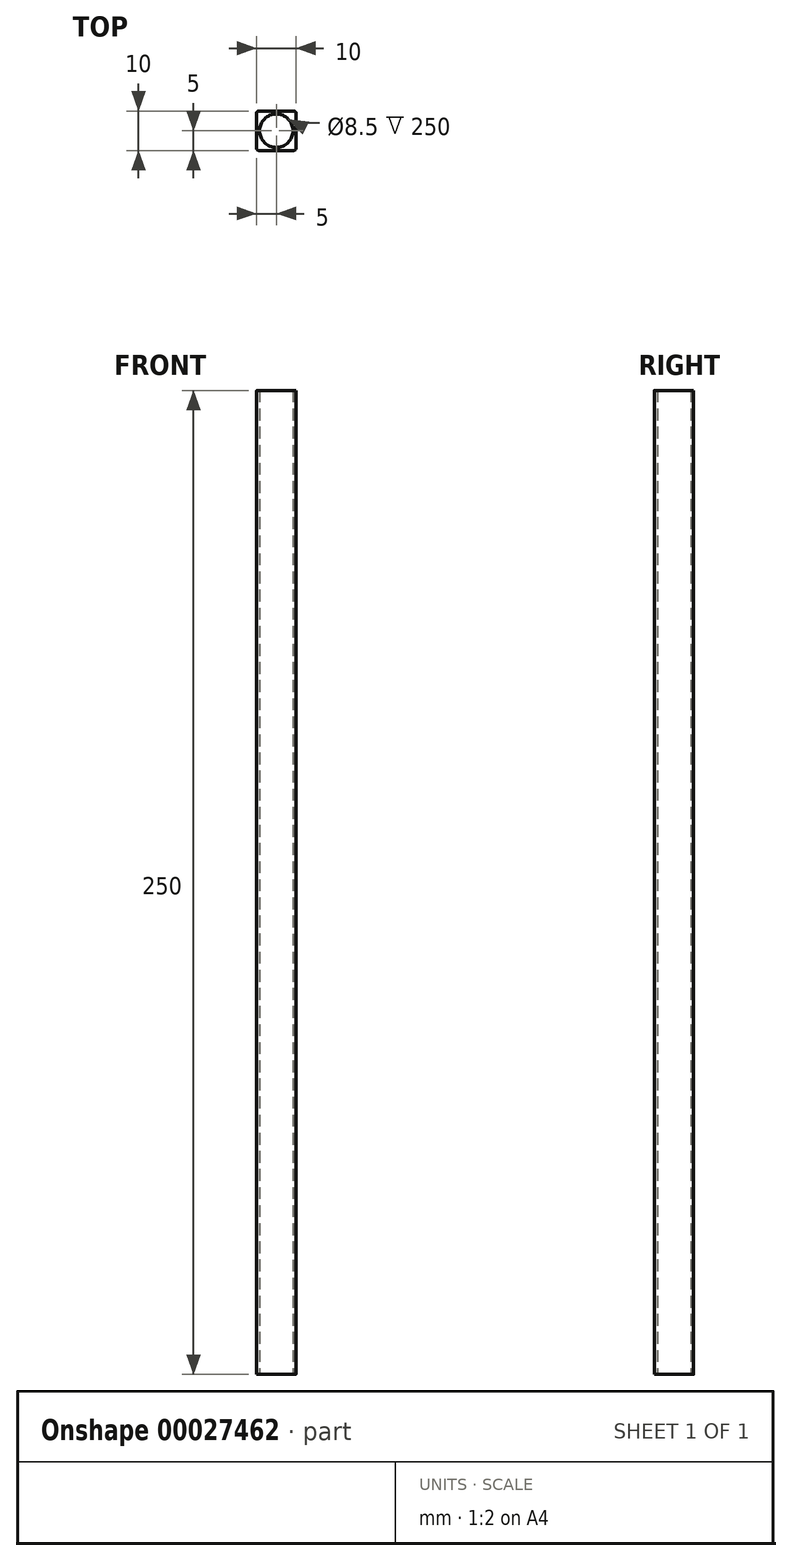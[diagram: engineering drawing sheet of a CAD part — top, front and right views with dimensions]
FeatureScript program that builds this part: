
annotation { "Feature Type Name" : "Feature", "Feature Type Description" : "" }
export const myFeature = defineFeature(function(context is Context, id is Id, definition is map)
    precondition{}
    {
        {
            var Q0;
            Q0=qCreatedBy(makeId("Top.planeOp"),FACE);
            var sketch = newSketch(context, id + "F0", { "sketchPlane" : qUnion([Q0])});
            skCircle(sketch, "E0", {"center": v(0, 0) * mm, "radius": 4.25 * mm});
            skLineSegment(sketch, "E1.rect.bottom", {"start": v(4.5, 5) * mm, "end": v(-4.5, 5) * mm});
            skLineSegment(sketch, "E1.rect.top", {"start": v(4.5, -5) * mm, "end": v(-4.5, -5) * mm});
            skLineSegment(sketch, "E1.rect.left", {"start": v(5, 4.5) * mm, "end": v(5, -4.5) * mm});
            skLineSegment(sketch, "E1.rect.right", {"start": v(-5, 4.5) * mm, "end": v(-5, -4.5) * mm});
            skPoint(sketch, "E2.visualSharp", {"position": v(-5, 5) * mm});
            skArc(sketch, "E2.filletArc", {"start": v(-4.5, 5) * mm, "mid": v(-4.85, 4.85) * mm, "end": v(-5, 4.5) * mm});
            skPoint(sketch, "E3.visualSharp", {"position": v(5, 5) * mm});
            skArc(sketch, "E3.filletArc", {"start": v(5, 4.5) * mm, "mid": v(4.85, 4.85) * mm, "end": v(4.5, 5) * mm});
            skPoint(sketch, "E4.visualSharp", {"position": v(5, -5) * mm});
            skArc(sketch, "E4.filletArc", {"start": v(4.5, -5) * mm, "mid": v(4.85, -4.85) * mm, "end": v(5, -4.5) * mm});
            skPoint(sketch, "E5.visualSharp", {"position": v(-5, -5) * mm});
            skArc(sketch, "E5.filletArc", {"start": v(-5, -4.5) * mm, "mid": v(-4.85, -4.85) * mm, "end": v(-4.5, -5) * mm});
            skSolve(sketch);
        }
        {
            var Q0;
            Q0=qSketchRegion(id+"F0",true);
            extrude(context, id + "F1", {"entities" : qUnion([Q0]), "depth" : 250 * mm});
        }
    });
